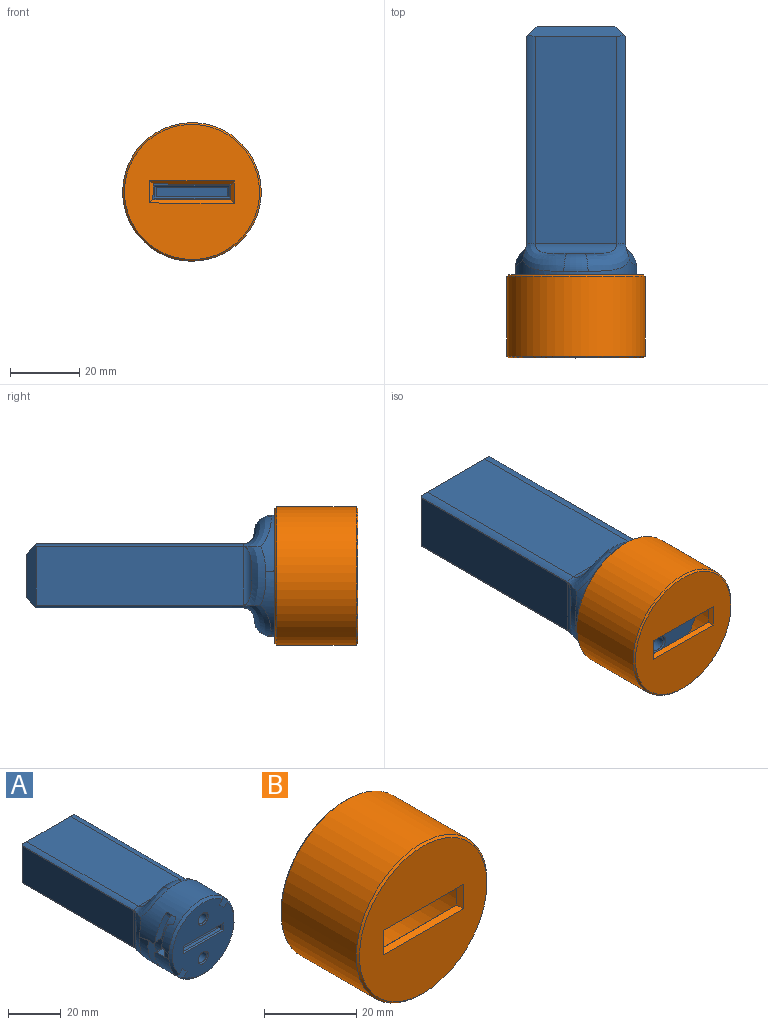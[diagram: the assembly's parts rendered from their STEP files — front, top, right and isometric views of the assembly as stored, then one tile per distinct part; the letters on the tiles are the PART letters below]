
ASSEMBLY  parts=2 mates=1
PART A: 106 faces, bbox 35.2x86x38.1 mm
  f0: plane 4.98x0.25mm, normal (0,1,0), area 0.8mm2, adj f85,f92
  f1: plane 4.98x0.25mm, normal (0,1,0), area 0.8mm2, adj f82,f97
  f2: cylinder r=17.5mm len=35mm, axis (0,-1,0), area 1327.5mm2, adj f3,f4,f6,f7,f37,f38,f40,f41
  f3: plane 10.14x7.93mm, normal (0,-1,0), area 36.2mm2, adj f2,f36,f61,f68
  f4: plane 10.14x7.93mm, normal (0,-1,0), area 36.2mm2, adj f2,f39,f58,f69
  f5: plane 33x33mm, normal (0,-1,0), area 715mm2, adj f6,f7,f28,f29,f32,f33,f34,f35
  f6: cone r=16.5mm half-angle=45deg, axis (0,1,0), area 70.6mm2, adj f2,f5,f38,f41
  f7: cone r=16.5mm half-angle=45deg, axis (0,1,0), area 70.6mm2, adj f2,f5,f37,f40
  f8: plane 76x20.5mm, normal (0,0,1), area 1558mm2, adj f9,f11,f12,f16
  f9: plane 81.3x10.5mm, normal (-1,0,0), area 822.8mm2, adj f8,f10,f12,f13,f14,f15,f16,f17
  f10: plane 76x20.5mm, normal (0,0,-1), area 1558mm2, adj f9,f11,f12,f13
  f11: plane 81.3x10.5mm, normal (1,0,0), area 822.8mm2, adj f8,f10,f12,f13,f14,f15,f16,f17
  f12: plane 20.5x10.5mm, normal (0,-1,0), area 215.3mm2, adj f8,f9,f10,f11
  f13: plane 20.5x3.15mm, normal (0,0.82,-0.57), area 78.8mm2, adj f9,f10,f11,f17
  f14: plane 20.5x1.46mm, normal (0,0,-1), area 29.9mm2, adj f9,f11,f17,f34
  f15: plane 20.5x1.46mm, normal (0,0,1), area 29.9mm2, adj f9,f11,f18,f33
  f16: plane 20.5x3.15mm, normal (0,0.82,0.57), area 78.8mm2, adj f8,f9,f11,f18
  f17: cylinder r=2mm len=20.5mm, axis (-1,0,0), area 39.4mm2, adj f9,f11,f13,f14
  f18: cylinder r=2mm len=20.5mm, axis (-1,0,0), area 39.4mm2, adj f9,f11,f15,f16
  f19: plane 22.5x12.5mm, normal (0,1,0), area 281.2mm2, adj f102,f103,f104,f105
  f20: plane 59.8x23.51mm, normal (0,0,1), area 1406mm2, adj f85,f88,f93,f102
  f21: plane 59.8x23.51mm, normal (0,0,-1), area 1406mm2, adj f82,f91,f100,f105
  f22: plane 59.8x16.82mm, normal (-1,0,0), area 1005.6mm2, adj f84,f86,f89,f104
  f23: plane 59.8x16.82mm, normal (1,0,0), area 1005.6mm2, adj f83,f96,f101,f103
  f24: cylinder r=2.25mm len=9mm, axis (0,-1,0), area 127.2mm2, adj f29,f30
  f25: plane 3.5x3.5mm, normal (0,-1,0), area 9.6mm2, adj f30
  f26: cylinder r=2.25mm len=9mm, axis (0,-1,0), area 127.2mm2, adj f28,f31
  f27: plane 3.5x3.5mm, normal (0,-1,0), area 9.6mm2, adj f31
  f28: cone r=2.25mm half-angle=45deg, axis (0,-1,0), area 11.1mm2, adj f5,f26
  f29: cone r=2.25mm half-angle=45deg, axis (0,-1,0), area 11.1mm2, adj f5,f24
  f30: cone r=1.75mm half-angle=45deg, axis (0,-1,0), area 8.9mm2, adj f24,f25
  f31: cone r=1.75mm half-angle=45deg, axis (0,-1,0), area 8.9mm2, adj f26,f27
  f32: plane 3.5x0.5mm, normal (0.71,-0.71,0), area 2.1mm2, adj f5,f11,f33,f34
  f33: plane 21.5x0.5mm, normal (0,-0.71,0.71), area 14.8mm2, adj f5,f15,f32,f35
  f34: plane 21.5x0.5mm, normal (0,-0.71,-0.71), area 14.8mm2, adj f5,f14,f32,f35
  f35: plane 3.5x0.5mm, normal (-0.71,-0.71,0), area 2.1mm2, adj f5,f9,f33,f34
  f36: cylinder r=14mm len=22.12mm, axis (0,1,0), area 147.7mm2, adj f3,f5,f37,f38,f42,f43,f46,f47
  f37: plane 12.19x2.49mm, normal (-0.71,0,0.71), area 42mm2, adj f2,f5,f7,f36,f62
  f38: plane 8.46x2.49mm, normal (0.71,0,-0.71), area 28.9mm2, adj f2,f5,f6,f36,f80
  f39: cylinder r=14mm len=22.12mm, axis (0,1,0), area 147.7mm2, adj f4,f5,f40,f41,f44,f45,f48,f49
  f40: plane 8.46x2.49mm, normal (-0.71,0,0.71), area 28.9mm2, adj f2,f5,f7,f39,f81
  f41: plane 12.19x2.49mm, normal (0.71,0,-0.71), area 42mm2, adj f2,f5,f6,f39,f59
  f42: plane 3.52x1.5mm, normal (0,1,0), area 5.3mm2, adj f2,f36,f64,f76
  f43: plane 3.79x3.52mm, normal (0,0,1), area 13.3mm2, adj f2,f36,f76,f77
  f44: plane 3.52x1.5mm, normal (0,1,0), area 5.3mm2, adj f2,f39,f66,f78
  f45: plane 3.79x3.52mm, normal (0,0,-1), area 13.3mm2, adj f2,f39,f78,f79
  f46: plane 3.54x3.54mm, normal (0,1,0), area 5.3mm2, adj f2,f36,f71,f72
  f47: plane 3.5x2.49mm, normal (-0.71,0,-0.71), area 12.3mm2, adj f2,f36,f68,f72
  f48: plane 3.54x3.54mm, normal (0,1,0), area 5.3mm2, adj f2,f39,f74,f75
  f49: plane 3.5x2.49mm, normal (0.71,0,0.71), area 12.3mm2, adj f2,f39,f69,f75
  f50: plane 7.53x5.63mm, normal (0,1,0), area 23.9mm2, adj f2,f39,f67,f73
  f51: plane 7.53x5.63mm, normal (0,1,0), area 23.9mm2, adj f2,f36,f65,f70
  f52: plane 7.59x5.64mm, normal (0,1,-0.09), area 24.1mm2, adj f2,f39,f79,f81
  f53: plane 3.52x1.5mm, normal (0,0,1), area 5.3mm2, adj f2,f39,f58,f60
  f54: plane 13.8x8.21mm, normal (0,-1,0.09), area 48.8mm2, adj f2,f39,f59,f60
  f55: plane 7.59x5.64mm, normal (0,1,0.09), area 24.1mm2, adj f2,f36,f77,f80
  f56: plane 3.52x1.5mm, normal (0,0,-1), area 5.3mm2, adj f2,f36,f61,f63
  f57: plane 13.8x8.21mm, normal (0,-1,-0.09), area 48.8mm2, adj f2,f36,f62,f63
  f58: cylinder r=1mm len=3.69mm, axis (-1,0,0), area 5.6mm2, adj f2,f4,f39,f53
  f59: cylinder r=1mm len=3.38mm, axis (0.71,0.06,0.71), area 5.7mm2, adj f2,f39,f41,f54
  f60: cylinder r=1mm len=3.59mm, axis (1,0,0), area 5.2mm2, adj f2,f39,f53,f54
  f61: cylinder r=1mm len=3.69mm, axis (1,0,0), area 5.6mm2, adj f2,f3,f36,f56
  f62: cylinder r=1mm len=3.38mm, axis (-0.71,0.06,-0.71), area 5.7mm2, adj f2,f36,f37,f57
  f63: cylinder r=1mm len=3.59mm, axis (-1,0,0), area 5.2mm2, adj f2,f36,f56,f57
  f64: cylinder r=1mm len=3.59mm, axis (-1,0,0), area 5.5mm2, adj f2,f36,f42,f65
  f65: cylinder r=1mm len=3.69mm, axis (1,0,0), area 5.6mm2, adj f2,f36,f51,f64
  f66: cylinder r=1mm len=3.59mm, axis (1,0,0), area 5.5mm2, adj f2,f39,f44,f67
  f67: cylinder r=1mm len=3.69mm, axis (-1,0,0), area 5.6mm2, adj f2,f39,f50,f66
  f68: cylinder r=1mm len=3.25mm, axis (0.71,0,-0.71), area 5.5mm2, adj f2,f3,f36,f47
  f69: cylinder r=1mm len=3.25mm, axis (-0.71,0,0.71), area 5.5mm2, adj f2,f4,f39,f49
  f70: cylinder r=1mm len=3.31mm, axis (-0.71,0,0.71), area 5.6mm2, adj f2,f36,f51,f71
  f71: cylinder r=1mm len=3.25mm, axis (0.71,0,-0.71), area 5.5mm2, adj f2,f36,f46,f70
  f72: cylinder r=1mm len=3.25mm, axis (-0.71,0,0.71), area 5.5mm2, adj f2,f36,f46,f47
  f73: cylinder r=1mm len=3.31mm, axis (0.71,0,-0.71), area 5.6mm2, adj f2,f39,f50,f74
  f74: cylinder r=1mm len=3.25mm, axis (-0.71,0,0.71), area 5.5mm2, adj f2,f39,f48,f73
  f75: cylinder r=1mm len=3.25mm, axis (0.71,0,-0.71), area 5.5mm2, adj f2,f39,f48,f49
  f76: cylinder r=1mm len=3.59mm, axis (1,0,0), area 5.5mm2, adj f2,f36,f42,f43
  f77: cylinder r=1mm len=3.67mm, axis (-1,0,0), area 5.2mm2, adj f2,f36,f43,f55
  f78: cylinder r=1mm len=3.59mm, axis (-1,0,0), area 5.5mm2, adj f2,f39,f44,f45
  f79: cylinder r=1mm len=3.67mm, axis (1,0,0), area 5.2mm2, adj f2,f39,f45,f52
  f80: cylinder r=1mm len=3.37mm, axis (0.71,-0.06,0.71), area 5.8mm2, adj f2,f36,f38,f55
  f81: cylinder r=1mm len=3.37mm, axis (-0.71,-0.06,-0.71), area 5.8mm2, adj f2,f39,f40,f52
  f82: cylinder r=3mm len=23.51mm, axis (-1,0,0), area 91.2mm2, adj f1,f21,f94,f99
  f83: cylinder r=3mm len=16.82mm, axis (0,0,-1), area 28.8mm2, adj f23,f98
  f84: cylinder r=3mm len=16.82mm, axis (0,0,1), area 28.8mm2, adj f22,f87
  f85: cylinder r=3mm len=23.51mm, axis (1,0,0), area 91.2mm2, adj f0,f20,f90,f95
  f86: cylinder r=5mm len=59.8mm, axis (0,-1,0), area 10.6mm2, adj f22,f87,f88,f104
  f87: bspline ~23.54x7.69mm, area 78.2mm2, adj f2,f84,f86,f89,f90,f94
  f88: cylinder r=5mm len=60.24mm, axis (0,-1,0), area 156.5mm2, adj f20,f86,f90,f102,f104
  f89: cylinder r=5mm len=59.8mm, axis (0,-1,0), area 10.6mm2, adj f22,f87,f91,f104
  f90: bspline ~15.49x11.51mm, area 98.3mm2, adj f2,f85,f87,f88,f92
  f91: cylinder r=5mm len=60.24mm, axis (0,-1,0), area 156.5mm2, adj f21,f89,f94,f104,f105
  f92: torus R=12.5mm, axis (0,-1,0), area 49.4mm2, adj f0,f2,f90,f95
  f93: cylinder r=5mm len=60.24mm, axis (0,-1,0), area 156.5mm2, adj f20,f95,f96,f102,f103
  f94: bspline ~15.49x11.51mm, area 98.3mm2, adj f2,f82,f87,f91,f97
  f95: bspline ~15.49x11.51mm, area 98.3mm2, adj f2,f85,f92,f93,f98
  f96: cylinder r=5mm len=59.8mm, axis (0,-1,0), area 10.6mm2, adj f23,f93,f98,f103
  f97: torus R=12.5mm, axis (0,-1,0), area 49.4mm2, adj f1,f2,f94,f99
  f98: bspline ~23.54x7.69mm, area 78.2mm2, adj f2,f83,f95,f96,f99,f101
  f99: bspline ~15.49x11.51mm, area 98.3mm2, adj f2,f82,f97,f98,f100
  f100: cylinder r=5mm len=60.24mm, axis (0,-1,0), area 156.5mm2, adj f21,f99,f101,f103,f105
  f101: cylinder r=5mm len=59.8mm, axis (0,-1,0), area 10.6mm2, adj f23,f98,f100,f103
  f102: plane 27.84x3.22mm, normal (0,0.71,0.71), area 107.1mm2, adj f19,f20,f88,f93,f103,f104
  f103: plane 17.62x3.01mm, normal (0.71,0.71,0), area 65.4mm2, adj f19,f23,f93,f96,f100,f101,f102,f105
  f104: plane 17.62x3.01mm, normal (-0.71,0.71,0), area 65.4mm2, adj f19,f22,f86,f88,f89,f91,f102,f105
  f105: plane 27.84x3.22mm, normal (0,0.71,-0.71), area 107.1mm2, adj f19,f21,f91,f100,f103,f104
PART B: 22 faces, bbox 40x24x40 mm
  f0: cylinder r=18mm len=36mm, axis (0,-1,0), area 2417.4mm2, adj f1,f15,f17,f18
  f1: plane 36x36mm, normal (0,1,0), area 858.6mm2, adj f0,f4,f5,f7,f8
  f2: cylinder r=20mm len=40mm, axis (0,1,0), area 2890.3mm2, adj f13,f14
  f3: plane 39x39mm, normal (0,-1,0), area 1035.3mm2, adj f6,f9,f10,f11,f13
  f4: plane 6.5x1mm, normal (0.71,0.71,0), area 7.8mm2, adj f1,f5,f6,f7
  f5: plane 24.5x1mm, normal (0,0.71,-0.71), area 33.2mm2, adj f1,f4,f8,f9
  f6: plane 6.5x1mm, normal (0.71,-0.71,0), area 7.8mm2, adj f3,f4,f9,f10
  f7: plane 24.5x1mm, normal (0,0.71,0.71), area 33.2mm2, adj f1,f4,f8,f10
  f8: plane 6.5x1mm, normal (-0.71,0.71,0), area 7.8mm2, adj f1,f5,f7,f11
  f9: plane 24.5x1mm, normal (0,-0.71,-0.71), area 33.2mm2, adj f3,f5,f6,f11
  f10: plane 24.5x1mm, normal (0,-0.71,0.71), area 33.2mm2, adj f3,f6,f7,f11
  f11: plane 6.5x1mm, normal (-0.71,-0.71,0), area 7.8mm2, adj f3,f8,f9,f10
  f12: plane 39x39mm, normal (0,1,0), area 119.4mm2, adj f14,f15
  f13: cone r=19.5mm half-angle=45deg, axis (0,1,0), area 87.7mm2, adj f2,f3
  f14: cone r=20mm half-angle=45deg, axis (0,-1,0), area 87.7mm2, adj f2,f12
  f15: cone r=18.5mm half-angle=45deg, axis (0,1,0), area 81.1mm2, adj f0,f12
  f16: plane 2x2mm, normal (1,0,0), area 3.1mm2, adj f21
  f17: cylinder r=1.5mm len=3.5mm, axis (1,0,0), area 32.7mm2, adj f0,f21
  f18: cylinder r=1.5mm len=3.5mm, axis (-1,0,0), area 32.7mm2, adj f0,f20
  f19: plane 2x2mm, normal (-1,0,0), area 3.1mm2, adj f20
  f20: torus R=1mm, axis (-1,0,0), area 6.5mm2, adj f18,f19
  f21: torus R=1mm, axis (1,0,0), area 6.5mm2, adj f16,f17
PLACE A at identity fixed
PLACE B rot(axis=(0,1,0),0.4deg) t=(0,0,0)mm
MATE cylindrical B.f2 <-> A.f6  axis (0,-1,0) through (0,-13.8,0)mm
